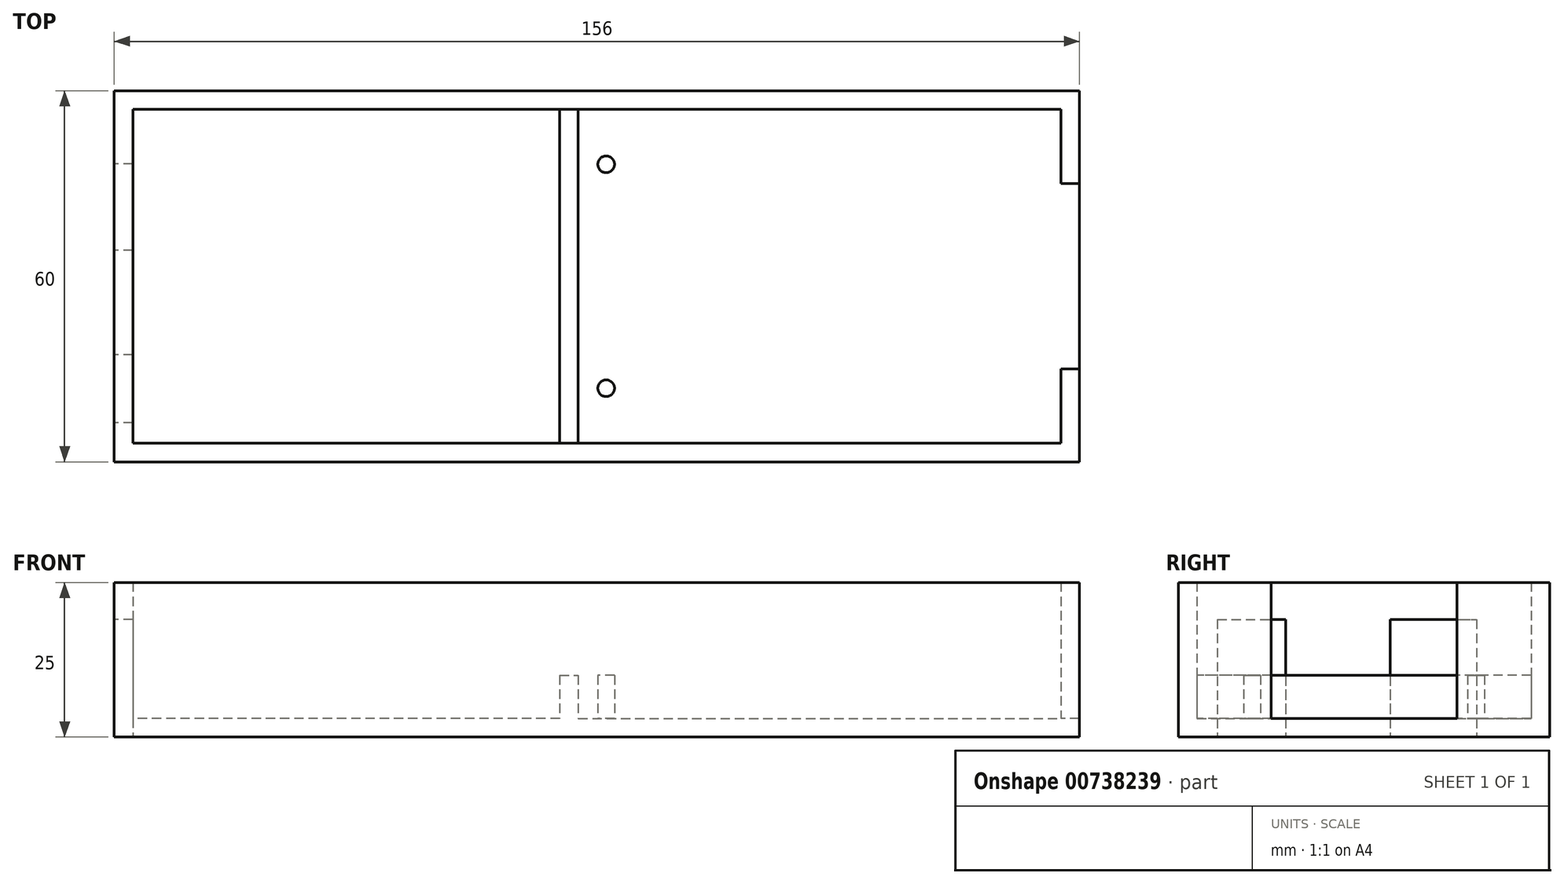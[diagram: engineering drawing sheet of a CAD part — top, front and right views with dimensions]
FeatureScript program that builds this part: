
annotation { "Feature Type Name" : "Feature", "Feature Type Description" : "" }
export const myFeature = defineFeature(function(context is Context, id is Id, definition is map)
    precondition{}
    {
        {
            var Q0;
            Q0=qCreatedBy(makeId("Top.planeOp"),FACE);
            var sketch = newSketch(context, id + "F0", { "sketchPlane" : qUnion([Q0])});
            skLineSegment(sketch, "E0", {"start": v(-69, 0) * mm, "end": v(-69, 54) * mm});
            skLineSegment(sketch, "E1", {"start": v(-69, 54) * mm, "end": v(0, 54) * mm});
            skLineSegment(sketch, "E2", {"start": v(0, 54) * mm, "end": v(0, 0) * mm});
            skLineSegment(sketch, "E3", {"start": v(0, 0) * mm, "end": v(-69, 0) * mm});
            skLineSegment(sketch, "E4", {"start": v(0, 0) * mm, "end": v(51, 0) * mm});
            skLineSegment(sketch, "E5", {"start": v(51, 0) * mm, "end": v(51, 54) * mm});
            skLineSegment(sketch, "E6", {"start": v(51, 54) * mm, "end": v(0, 54) * mm});
            skPoint(sketch, "E7", {"position": v(-69, 45.2) * mm});
            skPoint(sketch, "E8", {"position": v(-69, 31.2) * mm});
            skPoint(sketch, "E9", {"position": v(-69, 3.3) * mm});
            skPoint(sketch, "E10", {"position": v(-69, 14.3) * mm});
            skLineSegment(sketch, "E11", {"start": v(51, 54) * mm, "end": v(81, 54) * mm});
            skLineSegment(sketch, "E12", {"start": v(81, 54) * mm, "end": v(81, 0) * mm});
            skLineSegment(sketch, "E13", {"start": v(81, 0) * mm, "end": v(51, 0) * mm});
            skLineSegment(sketch, "E14.0", {"start": v(-72, -3) * mm, "end": v(-72, 57) * mm});
            skLineSegment(sketch, "E14.1", {"start": v(0, -3) * mm, "end": v(-72, -3) * mm});
            skLineSegment(sketch, "E14.2", {"start": v(-72, 57) * mm, "end": v(2.1, 57) * mm});
            skLineSegment(sketch, "E14.3", {"start": v(0, -3) * mm, "end": v(44, -3) * mm});
            skLineSegment(sketch, "E14.4", {"start": v(46.1, 57) * mm, "end": v(2.1, 57) * mm});
            skLineSegment(sketch, "E14.5", {"start": v(46.1, 57) * mm, "end": v(84, 57) * mm});
            skLineSegment(sketch, "E14.6", {"start": v(84, 57) * mm, "end": v(84, -3) * mm});
            skLineSegment(sketch, "E14.7", {"start": v(84, -3) * mm, "end": v(44, -3) * mm});
            skLineSegment(sketch, "E15", {"start": v(-69, 31.2) * mm, "end": v(-72, 31.2) * mm});
            skLineSegment(sketch, "E16", {"start": v(-69, 45.2) * mm, "end": v(-72, 45.2) * mm});
            skLineSegment(sketch, "E17", {"start": v(-69, 3.3) * mm, "end": v(-72, 3.3) * mm});
            skLineSegment(sketch, "E18", {"start": v(-69, 14.3) * mm, "end": v(-72, 14.3) * mm});
            skLineSegment(sketch, "E19.0", {"start": v(3, 54) * mm, "end": v(3, 0) * mm});
            skPoint(sketch, "E20", {"position": v(7.5, 45.1) * mm});
            skPoint(sketch, "E21", {"position": v(7.5, 8.9) * mm});
            skLineSegment(sketch, "E22", {"start": v(7.5, 45.1) * mm, "end": v(7.5, 54) * mm});
            skLineSegment(sketch, "E23", {"start": v(7.5, 8.9) * mm, "end": v(7.5, 0) * mm});
            skLineSegment(sketch, "E24", {"start": v(7.5, 0) * mm, "end": v(3, 0) * mm});
            skLineSegment(sketch, "E25", {"start": v(7.5, 54) * mm, "end": v(3, 54) * mm});
            skCircle(sketch, "E26", {"center": v(7.5, 8.9) * mm, "radius": 1.35 * mm});
            skCircle(sketch, "E27", {"center": v(7.5, 45.1) * mm, "radius": 1.35 * mm});
            skPoint(sketch, "E28", {"position": v(81, 42) * mm});
            skPoint(sketch, "E29", {"position": v(81, 12) * mm});
            skLineSegment(sketch, "E30", {"start": v(81, 42) * mm, "end": v(81, 54) * mm});
            skLineSegment(sketch, "E31", {"start": v(81, 12) * mm, "end": v(81, 0) * mm});
            skLineSegment(sketch, "E32", {"start": v(81, 42) * mm, "end": v(84, 42) * mm});
            skLineSegment(sketch, "E33", {"start": v(81, 12) * mm, "end": v(84, 12) * mm});
            skLineSegment(sketch, "E34", {"start": v(-69, 54) * mm, "end": v(-69, 57) * mm});
            skLineSegment(sketch, "E35", {"start": v(-69, 0) * mm, "end": v(-69, -3) * mm});
            skSolve(sketch);
        }
        {
            var Q0;
            Q0 = qSketchRegion(id + "F0", true);
            var Q1;
            {var subQ6=sQuery(id+"F0.wireOp",EDGE,"E1");Q1=makeQuery(id+"F0.imprint","IMPRINT",FACE,{"disambiguationData":[TD([[makeQuery(id+"F0.imprint","IMPRINT",EDGE,{"derivedFrom":subQ6}),-1.0]])]});}
            var Q2;
            Q2=makeQuery(id+"F0.imprint","IMPRINT",FACE,{"disambiguationData":[TD([[makeQuery(id+"F0.imprint","IMPRINT",EDGE,{"derivedFrom":sQuery(id+"F0.wireOp",EDGE,"E2")}),1.0]])]});
            var Q3;
            Q3=makeQuery(id+"F0.imprint","IMPRINT",FACE,{"disambiguationData":[TD([[makeQuery(id+"F0.imprint","IMPRINT",EDGE,{"derivedFrom":sQuery(id+"F0.wireOp",EDGE,"E5")}),-1.0]])]});
            var Q4;
            {var subQ0=sQuery(id+"F0.wireOp",EDGE,"E5");Q4=makeQuery(id+"F0.imprint","IMPRINT",FACE,{"disambiguationData":[TD([[makeQuery(id+"F0.imprint","IMPRINT",EDGE,{"derivedFrom":subQ0}),1.0]])]});}
            var Q5;
            Q5=makeQuery(id+"F0.imprint","IMPRINT",FACE,{"disambiguationData":[TD([[makeQuery(id+"F0.imprint","IMPRINT",EDGE,{"derivedFrom":sQuery(id+"F0.wireOp",EDGE,"E27")}),1.0]])]});
            var Q6;
            Q6=makeQuery(id+"F0.imprint","IMPRINT",FACE,{"disambiguationData":[TD([[makeQuery(id+"F0.imprint","IMPRINT",EDGE,{"derivedFrom":sQuery(id+"F0.wireOp",EDGE,"E26")}),1.0]])]});
            extrude(context, id + "F1", {"entities" : qUnion([Q0, Q1, Q2, Q3, Q4, Q5, Q6]), "depth" : 3 * mm, "offsetDistance" : 25 * mm});
        }
        {
            var Q0;
            {var subQ0=sQuery(id+"F0.wireOp",EDGE,"E15");Q0=makeQuery(id+"F0.imprint","IMPRINT",FACE,{"disambiguationData":[TD([[makeQuery(id+"F0.imprint","IMPRINT",EDGE,{"derivedFrom":subQ0}),1.0]])]});}
            var Q1;
            {var subQ5=sQuery(id+"F0.wireOp",EDGE,"E1");Q1=makeQuery(id+"F0.imprint","IMPRINT",FACE,{"disambiguationData":[TD([[makeQuery(id+"F0.imprint","IMPRINT",EDGE,{"derivedFrom":subQ5}),1.0]])]});}
            var Q2;
            {var subQ3=sQuery(id+"F0.wireOp",EDGE,"E3");Q2=makeQuery(id+"F0.imprint","IMPRINT",FACE,{"disambiguationData":[TD([[makeQuery(id+"F0.imprint","IMPRINT",EDGE,{"derivedFrom":subQ3}),1.0]])]});}
            var Q3;
            {var subQ0=sQuery(id+"F0.wireOp",EDGE,"E16");Q3=makeQuery(id+"F0.imprint","IMPRINT",FACE,{"disambiguationData":[TD([[makeQuery(id+"F0.imprint","IMPRINT",EDGE,{"derivedFrom":subQ0}),-1.0]])]});}
            var Q4;
            {var subQ0=sQuery(id+"F0.wireOp",EDGE,"E17");Q4=makeQuery(id+"F0.imprint","IMPRINT",FACE,{"disambiguationData":[TD([[makeQuery(id+"F0.imprint","IMPRINT",EDGE,{"derivedFrom":subQ0}),1.0]])]});}
            var Q5;
            {var subQ0=sQuery(id+"F0.wireOp",EDGE,"E17");Q5=makeQuery(id+"F0.imprint","IMPRINT",FACE,{"disambiguationData":[TD([[makeQuery(id+"F0.imprint","IMPRINT",EDGE,{"derivedFrom":subQ0}),-1.0]])]});}
            var Q6;
            {var subQ0=sQuery(id+"F0.wireOp",EDGE,"E15");Q6=makeQuery(id+"F0.imprint","IMPRINT",FACE,{"disambiguationData":[TD([[makeQuery(id+"F0.imprint","IMPRINT",EDGE,{"derivedFrom":subQ0}),-1.0]])]});}
            extrude(context, id + "F2", {"entities" : qUnion([Q0, Q1, Q2, Q3, Q4, Q5, Q6]), "depth" : 25 * mm, "offsetDistance" : 25 * mm});
        }
        {
            var Q0;
            {var subQ0=sQuery(id+"F0.wireOp",EDGE,"E2");Q0=makeQuery(id+"F0.imprint","IMPRINT",FACE,{"disambiguationData":[TD([[makeQuery(id+"F0.imprint","IMPRINT",EDGE,{"derivedFrom":subQ0}),1.0]])]});}
            var Q1;
            Q1=makeQuery(id+"F0.imprint","IMPRINT",FACE,{"disambiguationData":[TD([[makeQuery(id+"F0.imprint","IMPRINT",EDGE,{"derivedFrom":sQuery(id+"F0.wireOp",EDGE,"E27")}),1.0]])]});
            var Q2;
            Q2=makeQuery(id+"F0.imprint","IMPRINT",FACE,{"disambiguationData":[TD([[makeQuery(id+"F0.imprint","IMPRINT",EDGE,{"derivedFrom":sQuery(id+"F0.wireOp",EDGE,"E26")}),1.0]])]});
            extrude(context, id + "F3", {"entities" : qUnion([Q0, Q1, Q2]), "operationType" : NewBodyOperationType.ADD, "depth" : 10 * mm, "offsetDistance" : 25 * mm});
        }
        {
            var Q0;
            {var subQ0=sQuery(id+"F0.wireOp",EDGE,"E17");Q0=makeQuery(id+"F0.imprint","IMPRINT",FACE,{"disambiguationData":[TD([[makeQuery(id+"F0.imprint","IMPRINT",EDGE,{"derivedFrom":subQ0}),-1.0]])]});}
            var Q1;
            {var subQ0=sQuery(id+"F0.wireOp",EDGE,"E15");Q1=makeQuery(id+"F0.imprint","IMPRINT",FACE,{"disambiguationData":[TD([[makeQuery(id+"F0.imprint","IMPRINT",EDGE,{"derivedFrom":subQ0}),-1.0]])]});}
            extrude(context, id + "F4", {"entities" : qUnion([Q0, Q1]), "operationType" : NewBodyOperationType.REMOVE, "depth" : 19 * mm, "offsetDistance" : 25 * mm});
        }
    });
